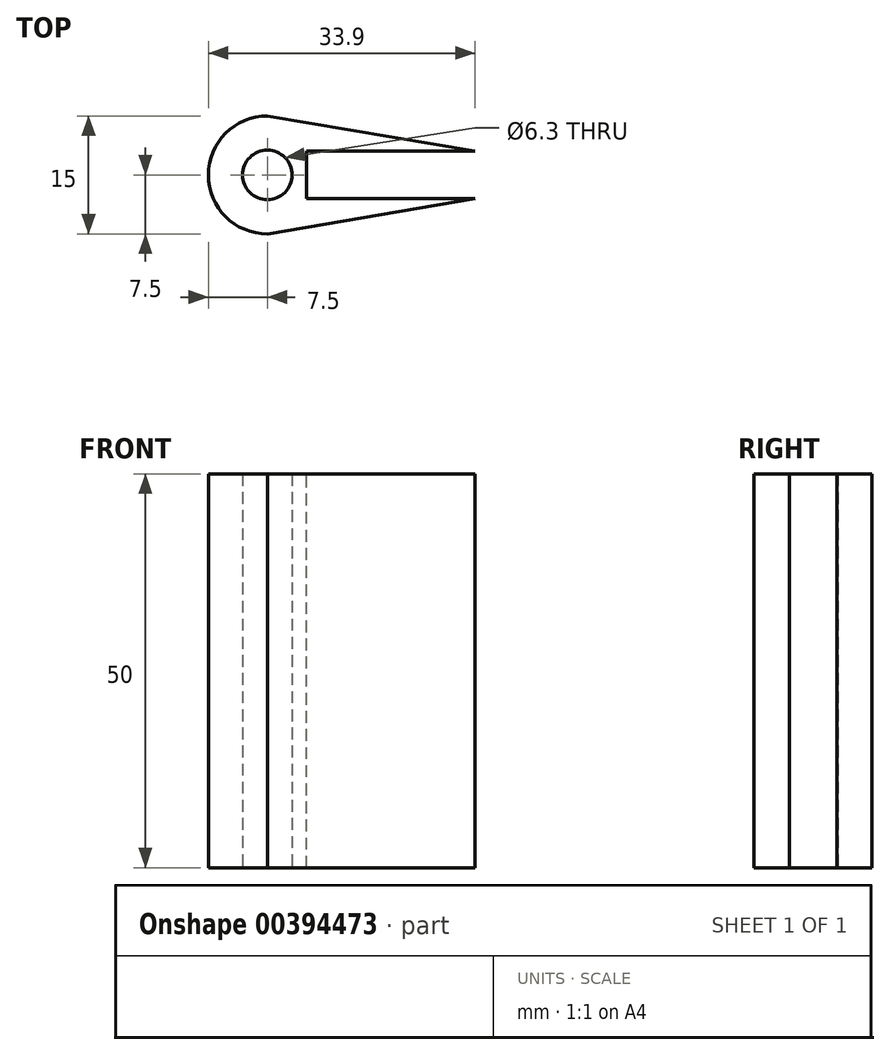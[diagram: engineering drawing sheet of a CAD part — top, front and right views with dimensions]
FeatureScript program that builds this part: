
annotation { "Feature Type Name" : "Feature", "Feature Type Description" : "" }
export const myFeature = defineFeature(function(context is Context, id is Id, definition is map)
    precondition{}
    {
        {
            var Q0;
            Q0=qCreatedBy(makeId("Top.planeOp"),FACE);
            var sketch = newSketch(context, id + "F0", { "sketchPlane" : qUnion([Q0])});
            skCircle(sketch, "E0", {"center": v(0, 0) * mm, "radius": 3.15 * mm});
            skCircle(sketch, "E1", {"center": v(0, 0) * mm, "radius": 7.5 * mm});
            skLineSegment(sketch, "E2", {"start": v(44, 0) * mm, "end": v(0, 7.5) * mm});
            skLineSegment(sketch, "E3", {"start": v(44, 0) * mm, "end": v(0, -7.5) * mm});
            skSolve(sketch);
        }
        {
            var Q0;
            Q0=makeQuery(id+"F0.imprint","IMPRINT",FACE,{"disambiguationData":[TD([[makeQuery(id+"F0.imprint","IMPRINT",EDGE,{"derivedFrom":sQuery(id+"F0.wireOp",EDGE,"E0")}),-1.0]])]});
            var Q1;
            {var subQ0=sQuery(id+"F0.wireOp",EDGE,"E2");var subQ1=sQuery(id+"F0.wireOp",EDGE,"E1");var subQ2=makeQuery(id+"F0.imprint","INTERSECT",VERTEX,{"disambiguationData":[OD(1.0)],"derivedFrom":[subQ1,subQ0]});Q1=makeQuery(id+"F0.imprint","IMPRINT",FACE,{"disambiguationData":[TD([[makeQuery(id+"F0.imprint","IMPRINT",EDGE,{"disambiguationData":[TD([[subQ2,1.0]])],"derivedFrom":subQ1}),-1.0]])]});}
            extrude(context, id + "F1", {"entities" : qUnion([Q0, Q1]), "depth" : 50 * mm});
        }
        {
            var Q0;
            Q0=makeQuery(id+"F1.opExtrude","CAP_FACE",FACE,{"disambiguationData":[OSD([sQuery(id+"F0.wireOp",EDGE,"E0"),sQuery(id+"F0.wireOp",EDGE,"E1"),sQuery(id+"F0.wireOp",EDGE,"E2"),sQuery(id+"F0.wireOp",EDGE,"E3")])],"isStart":false});
            var sketch = newSketch(context, id + "F2", { "sketchPlane" : qUnion([Q0])});
            skLineSegment(sketch, "E4.bottom", {"start": v(83, -3) * mm, "end": v(5, -3) * mm});
            skLineSegment(sketch, "E4.top", {"start": v(83, 3) * mm, "end": v(5, 3) * mm});
            skLineSegment(sketch, "E4.left", {"start": v(83, -3) * mm, "end": v(83, 3) * mm});
            skLineSegment(sketch, "E4.right", {"start": v(5, -3) * mm, "end": v(5, 3) * mm});
            skPoint(sketch, "E4.middle", {"position": v(44, 0) * mm});
            skSolve(sketch);
        }
        {
            var Q0;
            {var subQ5=sQuery(id+"F2.wireOp",EDGE,"E4.right");Q0=makeQuery(id+"F2.imprint","IMPRINT",FACE,{"disambiguationData":[TD([[makeQuery(id+"F2.imprint","IMPRINT",EDGE,{"derivedFrom":subQ5}),-1.0]])]});}
            extrude(context, id + "F3", {"entities" : qUnion([Q0]), "operationType" : NewBodyOperationType.REMOVE, "endBound" : BoundingType.THROUGH_ALL, "oppositeDirection" : true, "depth" : 25 * mm});
        }
    });
